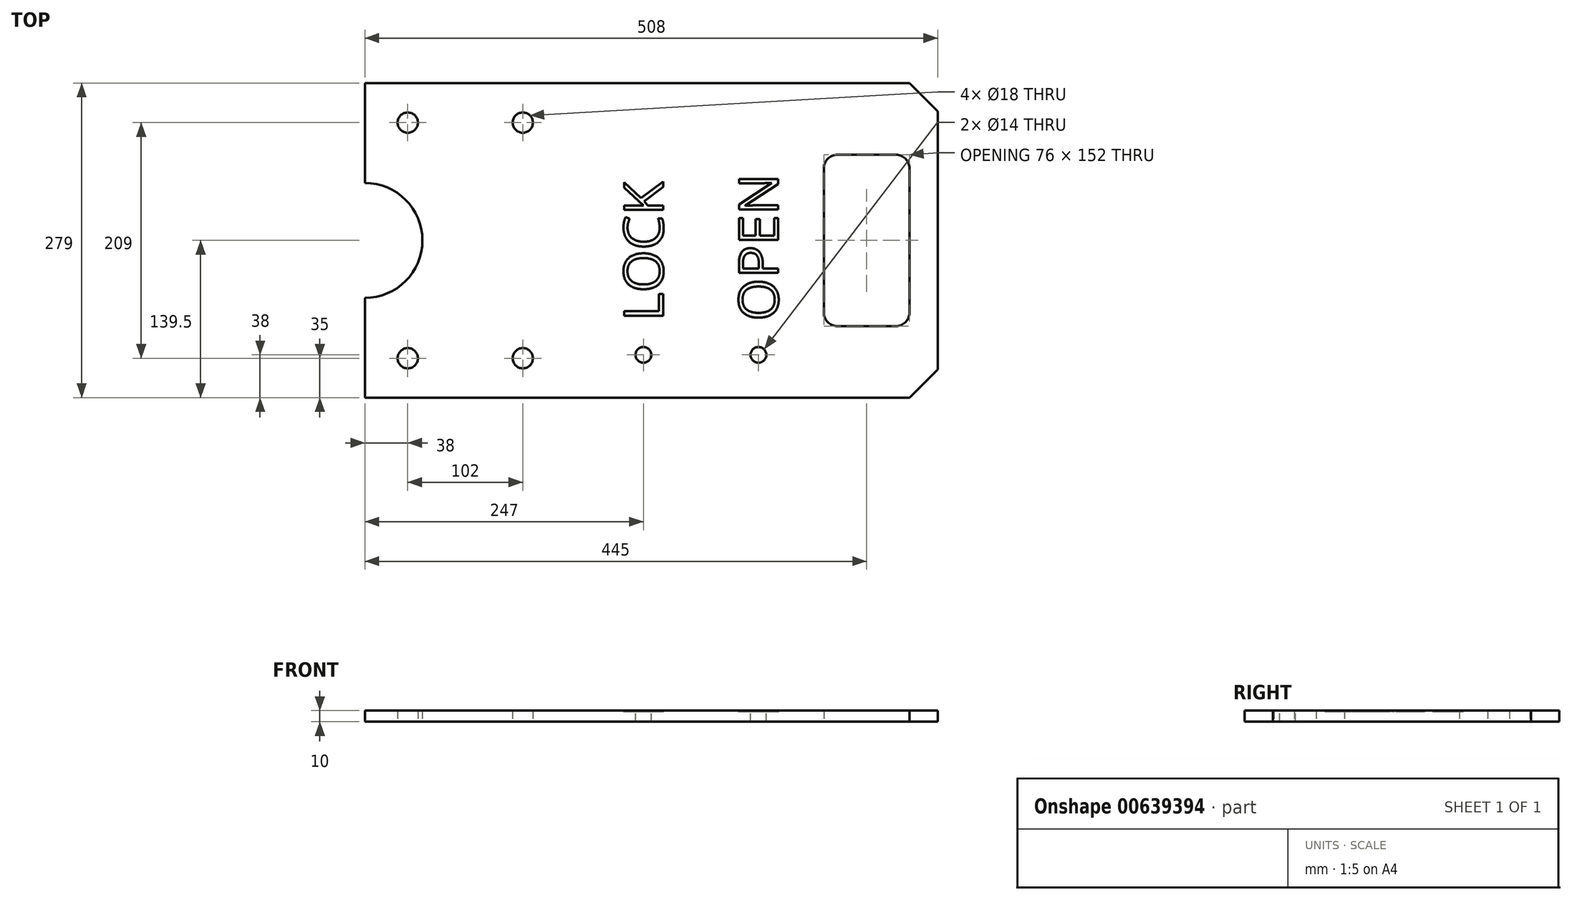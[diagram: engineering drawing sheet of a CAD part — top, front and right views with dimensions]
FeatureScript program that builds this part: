
annotation { "Feature Type Name" : "Feature", "Feature Type Description" : "" }
export const myFeature = defineFeature(function(context is Context, id is Id, definition is map)
    precondition{}
    {
        {
            var Q0;
            Q0=qCreatedBy(makeId("Top.planeOp"),FACE);
            var sketch = newSketch(context, id + "F0", { "sketchPlane" : qUnion([Q0])});
            skLineSegment(sketch, "E0.bottom", {"start": v(0, 0) * mm, "end": v(508, 0) * mm});
            skLineSegment(sketch, "E0.top", {"start": v(0, 279) * mm, "end": v(508, 279) * mm});
            skLineSegment(sketch, "E0.left", {"start": v(0, 0) * mm, "end": v(0, 88.5) * mm});
            skLineSegment(sketch, "E0.right", {"start": v(508, 0) * mm, "end": v(508, 279) * mm});
            skArc(sketch, "E1", {"start": v(0, 88.5) * mm, "mid": v(51, 139.5) * mm, "end": v(0, 190.5) * mm});
            skLineSegment(sketch, "E2.trimOffspring", {"start": v(0, 190.5) * mm, "end": v(0, 279) * mm});
            skLineSegment(sketch, "E3.0", {"start": v(483, 75.5) * mm, "end": v(483, 203.5) * mm});
            skPoint(sketch, "E4.endSnap0", {"position": v(483, 139.5) * mm});
            skLineSegment(sketch, "E5.0", {"start": v(471, 215.5) * mm, "end": v(419, 215.5) * mm});
            skLineSegment(sketch, "E6.0", {"start": v(471, 63.5) * mm, "end": v(419, 63.5) * mm});
            skLineSegment(sketch, "E7", {"start": v(407, 203.5) * mm, "end": v(407, 75.5) * mm});
            skPoint(sketch, "E8.orphan", {"position": v(483, 279) * mm});
            skPoint(sketch, "E9.orphan", {"position": v(483, 0) * mm});
            skPoint(sketch, "E10.visualSharp", {"position": v(407, 215.5) * mm});
            skArc(sketch, "E10.filletArc", {"start": v(419, 215.5) * mm, "mid": v(410.51, 211.99) * mm, "end": v(407, 203.5) * mm});
            skPoint(sketch, "E11.visualSharp", {"position": v(483, 215.5) * mm});
            skArc(sketch, "E11.filletArc", {"start": v(483, 203.5) * mm, "mid": v(479.49, 211.99) * mm, "end": v(471, 215.5) * mm});
            skPoint(sketch, "E12.visualSharp", {"position": v(407, 63.5) * mm});
            skArc(sketch, "E12.filletArc", {"start": v(407, 75.5) * mm, "mid": v(410.51, 67.01) * mm, "end": v(419, 63.5) * mm});
            skPoint(sketch, "E13.visualSharp", {"position": v(483, 63.5) * mm});
            skArc(sketch, "E13.filletArc", {"start": v(471, 63.5) * mm, "mid": v(479.49, 67.01) * mm, "end": v(483, 75.5) * mm});
            skCircle(sketch, "E14", {"center": v(140, 244) * mm, "radius": 9 * mm});
            skCircle(sketch, "E15", {"center": v(38, 244) * mm, "radius": 9 * mm});
            skCircle(sketch, "E16.MirrorC", {"center": v(140, 35) * mm, "radius": 9 * mm});
            skCircle(sketch, "E17.MirrorC", {"center": v(38, 35) * mm, "radius": 9 * mm});
            skSolve(sketch);
        }
        {
            var Q0;
            Q0=makeQuery(id+"F0.imprint","IMPRINT",FACE,{"disambiguationData":[TD([[makeQuery(id+"F0.imprint","IMPRINT",EDGE,{"derivedFrom":sQuery(id+"F0.wireOp",EDGE,"E0.bottom")}),1.0]])]});
            extrude(context, id + "F1", {"entities" : qUnion([Q0]), "depth" : 10 * mm, "offsetDistance" : 25 * mm});
        }
        {
            var Q0;
            Q0=makeQuery(id+"F1.opExtrude","SWEPT_EDGE",EDGE,{"disambiguationData":[OSD([sQuery(id+"F0.wireOp",EDGE,"E0.bottom"),sQuery(id+"F0.wireOp",EDGE,"E0.right")])]});
            var Q1;
            Q1=makeQuery(id+"F1.opExtrude","SWEPT_EDGE",EDGE,{"disambiguationData":[OSD([sQuery(id+"F0.wireOp",EDGE,"E0.top"),sQuery(id+"F0.wireOp",EDGE,"E0.right")])]});
            chamfer(context, id + "F2", {"entities" : qUnion([Q0, Q1]), "width" : 25 * mm, "tangentPropagation" : true});
        }
        {
            var Q0;
            Q0=makeQuery(id+"F1.opExtrude","CAP_FACE",FACE,{"disambiguationData":[OSD([sQuery(id+"F0.wireOp",EDGE,"E0.bottom"),sQuery(id+"F0.wireOp",EDGE,"E0.top"),sQuery(id+"F0.wireOp",EDGE,"E0.left"),sQuery(id+"F0.wireOp",EDGE,"E0.right"),sQuery(id+"F0.wireOp",EDGE,"E1"),sQuery(id+"F0.wireOp",EDGE,"E2.trimOffspring"),sQuery(id+"F0.wireOp",EDGE,"E3.0"),sQuery(id+"F0.wireOp",EDGE,"E5.0"),sQuery(id+"F0.wireOp",EDGE,"E6.0"),sQuery(id+"F0.wireOp",EDGE,"E7"),sQuery(id+"F0.wireOp",EDGE,"E10.filletArc"),sQuery(id+"F0.wireOp",EDGE,"E11.filletArc"),sQuery(id+"F0.wireOp",EDGE,"E12.filletArc"),sQuery(id+"F0.wireOp",EDGE,"E13.filletArc"),sQuery(id+"F0.wireOp",EDGE,"E14"),sQuery(id+"F0.wireOp",EDGE,"E15"),sQuery(id+"F0.wireOp",EDGE,"E16.MirrorC"),sQuery(id+"F0.wireOp",EDGE,"E17.MirrorC")])],"isStart":false});
            var sketch = newSketch(context, id + "F3", { "sketchPlane" : qUnion([Q0])});
            skLineSegment(sketch, "E18.0", {"start": v(0, 0) * mm, "end": v(483, 0) * mm});
            skLineSegment(sketch, "E19.0", {"start": v(508, 25) * mm, "end": v(508, 254) * mm});
            skCircle(sketch, "E20", {"center": v(349, 38) * mm, "radius": 7 * mm});
            skCircle(sketch, "E21", {"center": v(247, 38) * mm, "radius": 7 * mm});
            skSolve(sketch);
        }
        {
            var Q0;
            Q0=makeQuery(id+"F3.imprint","IMPRINT",FACE,{"disambiguationData":[TD([[makeQuery(id+"F3.imprint","IMPRINT",EDGE,{"derivedFrom":sQuery(id+"F3.wireOp",EDGE,"E21")}),1.0]])]});
            var Q1;
            Q1=makeQuery(id+"F3.imprint","IMPRINT",FACE,{"disambiguationData":[TD([[makeQuery(id+"F3.imprint","IMPRINT",EDGE,{"derivedFrom":sQuery(id+"F3.wireOp",EDGE,"E20")}),1.0]])]});
            extrude(context, id + "F4", {"entities" : qUnion([Q0, Q1]), "operationType" : NewBodyOperationType.REMOVE, "endBound" : BoundingType.UP_TO_NEXT, "oppositeDirection" : true, "depth" : 25 * mm, "offsetDistance" : 25 * mm});
        }
        {
            var Q0;
            Q0=makeQuery(id+"F1.opExtrude","CAP_FACE",FACE,{"disambiguationData":[OSD([sQuery(id+"F0.wireOp",EDGE,"E0.bottom"),sQuery(id+"F0.wireOp",EDGE,"E0.top"),sQuery(id+"F0.wireOp",EDGE,"E0.left"),sQuery(id+"F0.wireOp",EDGE,"E0.right"),sQuery(id+"F0.wireOp",EDGE,"E1"),sQuery(id+"F0.wireOp",EDGE,"E2.trimOffspring"),sQuery(id+"F0.wireOp",EDGE,"E3.0"),sQuery(id+"F0.wireOp",EDGE,"E5.0"),sQuery(id+"F0.wireOp",EDGE,"E6.0"),sQuery(id+"F0.wireOp",EDGE,"E7"),sQuery(id+"F0.wireOp",EDGE,"E10.filletArc"),sQuery(id+"F0.wireOp",EDGE,"E11.filletArc"),sQuery(id+"F0.wireOp",EDGE,"E12.filletArc"),sQuery(id+"F0.wireOp",EDGE,"E13.filletArc"),sQuery(id+"F0.wireOp",EDGE,"E14"),sQuery(id+"F0.wireOp",EDGE,"E15"),sQuery(id+"F0.wireOp",EDGE,"E16.MirrorC"),sQuery(id+"F0.wireOp",EDGE,"E17.MirrorC")])],"isStart":false});
            var sketch = newSketch(context, id + "F5", { "sketchPlane" : qUnion([Q0])});
            skText(sketch, "E22", { "text": "LOCK", "fontName": "OpenSans-Regular.ttf"});
            skLineSegment(sketch, "E23", {"start": v(247, 38) * mm, "end": v(247, 68) * mm, "construction": true});
            skLineSegment(sketch, "E24", {"start": v(247, 68) * mm, "end": v(247, 64.6) * mm});
            skLineSegment(sketch, "E25", {"start": v(349, 38) * mm, "end": v(349, 68) * mm, "construction": true});
            skText(sketch, "E26", { "text": "OPEN", "fontName": "OpenSans-Regular.ttf"});
            const initialGuessF5  = {"E22": [0.2645, 0.068, 0, 1, 0.035], "E26": [0.3665, 0.068, 0, 1, 0.035]};
            skSetInitialGuess(sketch, initialGuessF5);
            skSolve(sketch);
        }
        {
            var Q0;
            Q0=makeQuery(id+"F5.imprint","IMPRINT",FACE,{"disambiguationData":[TD([[makeQuery(id+"F5.imprint","IMPRINT",EDGE,{"derivedFrom":sQuery(id+"F5.wireOp",EDGE,"E22.sketch_text.stroke-6")}),-1.0]])]});
            var Q1;
            Q1=makeQuery(id+"F5.imprint","IMPRINT",FACE,{"disambiguationData":[TD([[makeQuery(id+"F5.imprint","IMPRINT",EDGE,{"derivedFrom":sQuery(id+"F5.wireOp",EDGE,"E22.sketch_text.stroke-22")}),-1.0]])]});
            var Q2;
            Q2=makeQuery(id+"F5.imprint","IMPRINT",FACE,{"disambiguationData":[TD([[makeQuery(id+"F5.imprint","IMPRINT",EDGE,{"derivedFrom":sQuery(id+"F5.wireOp",EDGE,"E22.sketch_text.stroke-37")}),-1.0]])]});
            var Q3;
            Q3=makeQuery(id+"F5.imprint","IMPRINT",FACE,{"disambiguationData":[TD([[makeQuery(id+"F5.imprint","IMPRINT",EDGE,{"derivedFrom":sQuery(id+"F5.wireOp",EDGE,"E22.sketch_text.stroke-0")}),-1.0]])]});
            var Q4;
            Q4=makeQuery(id+"F5.imprint","IMPRINT",FACE,{"disambiguationData":[TD([[makeQuery(id+"F5.imprint","IMPRINT",EDGE,{"derivedFrom":sQuery(id+"F5.wireOp",EDGE,"E26.sketch_text.stroke-0")}),-1.0]])]});
            var Q5;
            Q5=makeQuery(id+"F5.imprint","IMPRINT",FACE,{"disambiguationData":[TD([[makeQuery(id+"F5.imprint","IMPRINT",EDGE,{"derivedFrom":sQuery(id+"F5.wireOp",EDGE,"E26.sketch_text.stroke-16")}),-1.0]])]});
            var Q6;
            Q6=makeQuery(id+"F5.imprint","IMPRINT",FACE,{"disambiguationData":[TD([[makeQuery(id+"F5.imprint","IMPRINT",EDGE,{"derivedFrom":sQuery(id+"F5.wireOp",EDGE,"E26.sketch_text.stroke-31")}),-1.0]])]});
            var Q7;
            Q7=makeQuery(id+"F5.imprint","IMPRINT",FACE,{"disambiguationData":[TD([[makeQuery(id+"F5.imprint","IMPRINT",EDGE,{"derivedFrom":sQuery(id+"F5.wireOp",EDGE,"E26.sketch_text.stroke-43")}),-1.0]])]});
            extrude(context, id + "F6", {"entities" : qUnion([Q0, Q1, Q2, Q3, Q4, Q5, Q6, Q7]), "operationType" : NewBodyOperationType.REMOVE, "oppositeDirection" : true, "depth" : 1 * mm, "offsetDistance" : 25 * mm});
        }
    });
